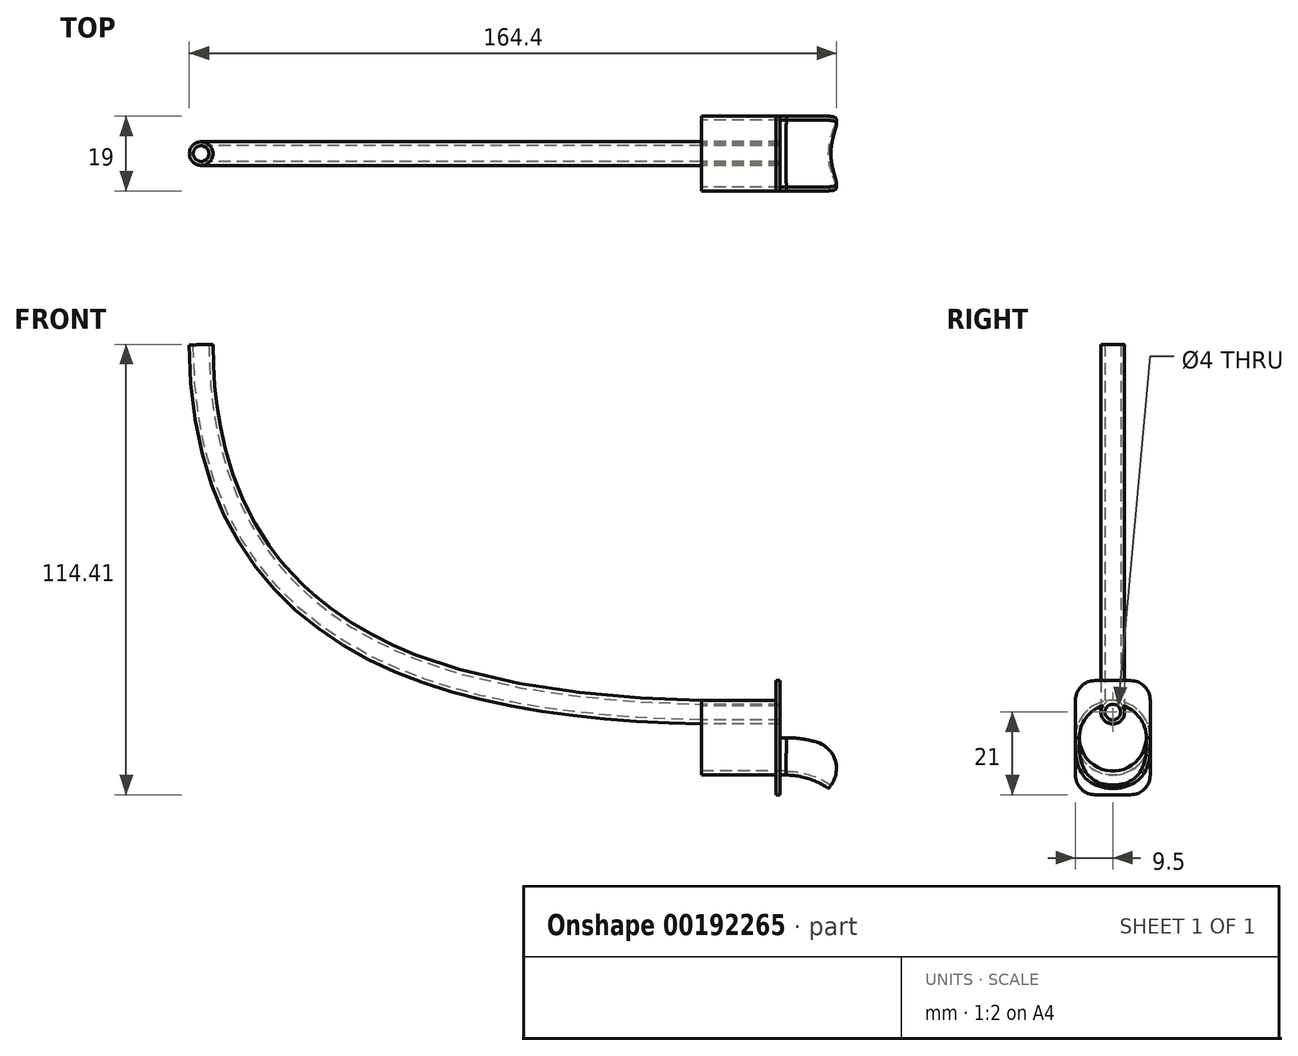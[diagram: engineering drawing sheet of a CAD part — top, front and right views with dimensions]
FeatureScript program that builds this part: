
annotation { "Feature Type Name" : "Feature", "Feature Type Description" : "" }
export const myFeature = defineFeature(function(context is Context, id is Id, definition is map)
    precondition{}
    {
        {
            var Q0;
            Q0=qCreatedBy(makeId("Right.planeOp"),FACE);
            var sketch = newSketch(context, id + "F0", { "sketchPlane" : qUnion([Q0])});
            skCircle(sketch, "E0", {"center": v(0, 0) * mm, "radius": 9.5 * mm});
            skCircle(sketch, "E1", {"center": v(0, 0) * mm, "radius": 8.5 * mm});
            skCircle(sketch, "E2", {"center": v(0, 6.5) * mm, "radius": 3 * mm});
            skCircle(sketch, "E3", {"center": v(0, 6.5) * mm, "radius": 2 * mm});
            skSolve(sketch);
        }
        {
            var Q0;
            Q0 = qSketchRegion(id + "F0", true);
            var Q1;
            {var subQ0=sQuery(id+"F0.wireOp",EDGE,"E3");Q1=makeQuery(id+"F0.imprint","IMPRINT",FACE,{"disambiguationData":[TD([[makeQuery(id+"F0.imprint","IMPRINT",EDGE,{"derivedFrom":subQ0}),-1.0]])]});}
            var Q2;
            Q2 = qSketchRegion(id + "F2", true);
            extrude(context, id + "F1", {"entities" : qUnion([Q0, Q1, Q2]), "depth" : 20 * mm});
        }
        {
            var Q0;
            Q0=qCreatedBy(makeId("Front.planeOp"),FACE);
            var sketch = newSketch(context, id + "F2", { "sketchPlane" : qUnion([Q0])});
            skFitSpline(sketch, "E4", {"points": [v(0, 13.58) * mm, v(-120, 100) * mm], "startDerivative": vector(-185.27, 4) * mm, "endDerivative": vector(0, 213.73) * mm});
            skLineSegment(sketch, "E5", {"start": v(-120, 100) * mm, "end": v(-120, 0) * mm, "construction": true});
            skLineSegment(sketch, "E6", {"start": v(0, 0) * mm, "end": v(0, 100) * mm, "construction": true});
            skLineSegment(sketch, "E7", {"start": v(0, 0) * mm, "end": v(-120, 0) * mm, "construction": true});
            skLineSegment(sketch, "E8", {"start": v(0, 100) * mm, "end": v(-120, 100) * mm, "construction": true});
            skSolve(sketch);
        }
        {
            var Q0;
            {var subQ0=sQuery(id+"F0.wireOp",EDGE,"E3");Q0=makeQuery(id+"F0.imprint","IMPRINT",FACE,{"disambiguationData":[TD([[makeQuery(id+"F0.imprint","IMPRINT",EDGE,{"derivedFrom":subQ0}),-1.0]])]});}
            var Q1;
            {var subQ0=sQuery(id+"F0.wireOp",EDGE,"E1");var subQ1=makeQuery(id+"F0.imprint","INTERSECT",VERTEX,{"derivedFrom":[subQ0,sQuery(id+"F0.wireOp",EDGE,"E3")]});Q1=makeQuery(id+"F0.imprint","IMPRINT",FACE,{"disambiguationData":[TD([[makeQuery(id+"F0.imprint","IMPRINT",EDGE,{"disambiguationData":[TD([[subQ1,1.0]])],"derivedFrom":subQ0}),-1.0]])]});}
            var Q2;
            Q2=makeQuery(id+"F1.opExtrude","CAP_EDGE",EDGE,{"disambiguationData":[OSD([sQuery(id+"F0.wireOp",EDGE,"E3")])],"isStart":true});
            var Q3;
            Q3=sQuery(id+"F2.wireOp",EDGE,"E4");
            sweep(context, id + "F3", {"profiles" : qUnion([Q0, Q1]), "surfaceProfiles" : qUnion([Q2]), "path" : qUnion([Q3])});
        }
        {
            var Q0;
            Q0=makeQuery(id+"F1.opExtrude","CAP_FACE",FACE,{"disambiguationData":[OSD([sQuery(id+"F0.wireOp",EDGE,"E0"),sQuery(id+"F0.wireOp",EDGE,"E1"),sQuery(id+"F0.wireOp",EDGE,"E2"),sQuery(id+"F0.wireOp",EDGE,"E3")])],"isStart":false});
            var sketch = newSketch(context, id + "F4", { "sketchPlane" : qUnion([Q0])});
            skCircle(sketch, "E9", {"center": v(0, 0) * mm, "radius": 9.5 * mm});
            skCircle(sketch, "E10", {"center": v(0, 0) * mm, "radius": 8.5 * mm});
            skLineSegment(sketch, "E11", {"start": v(-9.5, 0) * mm, "end": v(-8.5, 0) * mm});
            skLineSegment(sketch, "E12", {"start": v(8.5, 0) * mm, "end": v(9.5, 0) * mm});
            skLineSegment(sketch, "E13", {"start": v(0, 6.8) * mm, "end": v(0, -8.5) * mm, "construction": true});
            skLineSegment(sketch, "E14", {"start": v(0, -8.5) * mm, "end": v(0, -9.5) * mm, "construction": true});
            skSolve(sketch);
        }
        {
            var Q0;
            Q0=qCreatedBy(makeId("Front.planeOp"),FACE);
            var sketch = newSketch(context, id + "F5", { "sketchPlane" : qUnion([Q0])});
            skArc(sketch, "E15", {"start": v(32.36, -12.89) * mm, "mid": v(27.19, -10.4) * mm, "end": v(21.53, -9.5) * mm});
            skLineSegment(sketch, "E16", {"start": v(20, -9.5) * mm, "end": v(21.53, -9.5) * mm});
            skSolve(sketch);
        }
        {
            var Q0;
            {var subQ0=sQuery(id+"F4.wireOp",EDGE,"E11");Q0=makeQuery(id+"F4.imprint","IMPRINT",FACE,{"disambiguationData":[TD([[makeQuery(id+"F4.imprint","IMPRINT",EDGE,{"derivedFrom":subQ0}),-1.0]])]});}
            var Q1;
            Q1=sQuery(id+"F5.wireOp",EDGE,"E16");
            var Q2;
            Q2=sQuery(id+"F5.wireOp",EDGE,"E15");
            sweep(context, id + "F6", {"operationType" : NewBodyOperationType.ADD, "profiles" : qUnion([Q0]), "path" : qUnion([Q1, Q2])});
        }
        {
            var Q0;
            Q0=makeQuery(id+"F6.opSweep","CAP_EDGE",EDGE,{"disambiguationData":[OSD([sQuery(id+"F4.wireOp",EDGE,"E11"),sQuery(id+"F5.wireOp",VERTEX,"E15.start")])],"isStart":false});
            var Q1;
            Q1=makeQuery(id+"F6.opSweep","CAP_EDGE",EDGE,{"disambiguationData":[OSD([sQuery(id+"F4.wireOp",EDGE,"E12"),sQuery(id+"F5.wireOp",VERTEX,"E15.start")])],"isStart":false});
            var Q2;
            Q2=makeQuery(id+"F6.opSweep","CAP_EDGE",EDGE,{"disambiguationData":[OSD([sQuery(id+"F4.wireOp",EDGE,"E11"),sQuery(id+"F5.wireOp",VERTEX,"E16.start")])],"isStart":true});
            var Q3;
            Q3=makeQuery(id+"F6.opSweep","CAP_EDGE",EDGE,{"disambiguationData":[OSD([sQuery(id+"F4.wireOp",EDGE,"E12"),sQuery(id+"F5.wireOp",VERTEX,"E16.start")])],"isStart":true});
            fillet(context, id + "F7", {"entities" : qUnion([Q0, Q1, Q2, Q3]), "radius" : 7 * mm, "tangentPropagation" : true, "allowEdgeOverflow" : false});
        }
        {
            var Q0;
            Q0=makeQuery(id+"F1.opExtrude","CAP_FACE",FACE,{"disambiguationData":[OSD([sQuery(id+"F0.wireOp",EDGE,"E0"),sQuery(id+"F0.wireOp",EDGE,"E1"),sQuery(id+"F0.wireOp",EDGE,"E2"),sQuery(id+"F0.wireOp",EDGE,"E3")])],"isStart":false});
            var sketch = newSketch(context, id + "F8", { "sketchPlane" : qUnion([Q0])});
            skLineSegment(sketch, "E17.bottom", {"start": v(-9.5, 14.5) * mm, "end": v(9.5, 14.5) * mm});
            skLineSegment(sketch, "E17.top", {"start": v(-9.5, -14.5) * mm, "end": v(9.5, -14.5) * mm});
            skLineSegment(sketch, "E17.left", {"start": v(-9.5, 14.5) * mm, "end": v(-9.5, -14.5) * mm});
            skLineSegment(sketch, "E17.right", {"start": v(9.5, 14.5) * mm, "end": v(9.5, -14.5) * mm});
            skCircle(sketch, "E18", {"center": v(0, 0) * mm, "radius": 9.5 * mm});
            skSolve(sketch);
        }
        {
            var Q0;
            {var subQ6=sQuery(id+"F8.wireOp",EDGE,"E17.bottom");Q0=makeQuery(id+"F8.imprint","IMPRINT",FACE,{"disambiguationData":[TD([[makeQuery(id+"F8.imprint","IMPRINT",EDGE,{"derivedFrom":subQ6}),-1.0]])]});}
            var Q1;
            {var subQ0=sQuery(id+"F8.wireOp",EDGE,"E17.top");Q1=makeQuery(id+"F8.imprint","IMPRINT",FACE,{"disambiguationData":[TD([[makeQuery(id+"F8.imprint","IMPRINT",EDGE,{"derivedFrom":subQ0}),1.0]])]});}
            extrude(context, id + "F9", {"entities" : qUnion([Q0, Q1]), "operationType" : NewBodyOperationType.ADD, "oppositeDirection" : true, "depth" : 1 * mm});
        }
        {
            var Q0;
            Q0=makeQuery(id+"F9.opExtrude","SWEPT_EDGE",EDGE,{"disambiguationData":[OSD([sQuery(id+"F8.wireOp",EDGE,"E17.bottom"),sQuery(id+"F8.wireOp",EDGE,"E17.right")])]});
            var Q1;
            Q1=makeQuery(id+"F9.opExtrude","SWEPT_EDGE",EDGE,{"disambiguationData":[OSD([sQuery(id+"F8.wireOp",EDGE,"E17.bottom"),sQuery(id+"F8.wireOp",EDGE,"E17.left")])]});
            var Q2;
            Q2=makeQuery(id+"F9.opExtrude","SWEPT_EDGE",EDGE,{"disambiguationData":[OSD([sQuery(id+"F8.wireOp",EDGE,"E17.top"),sQuery(id+"F8.wireOp",EDGE,"E17.left")])]});
            var Q3;
            Q3=makeQuery(id+"F9.opExtrude","SWEPT_EDGE",EDGE,{"disambiguationData":[OSD([sQuery(id+"F8.wireOp",EDGE,"E17.top"),sQuery(id+"F8.wireOp",EDGE,"E17.right")])]});
            fillet(context, id + "F10", {"entities" : qUnion([Q0, Q1, Q2, Q3]), "radius" : 5 * mm, "tangentPropagation" : true, "allowEdgeOverflow" : false});
        }
    });
